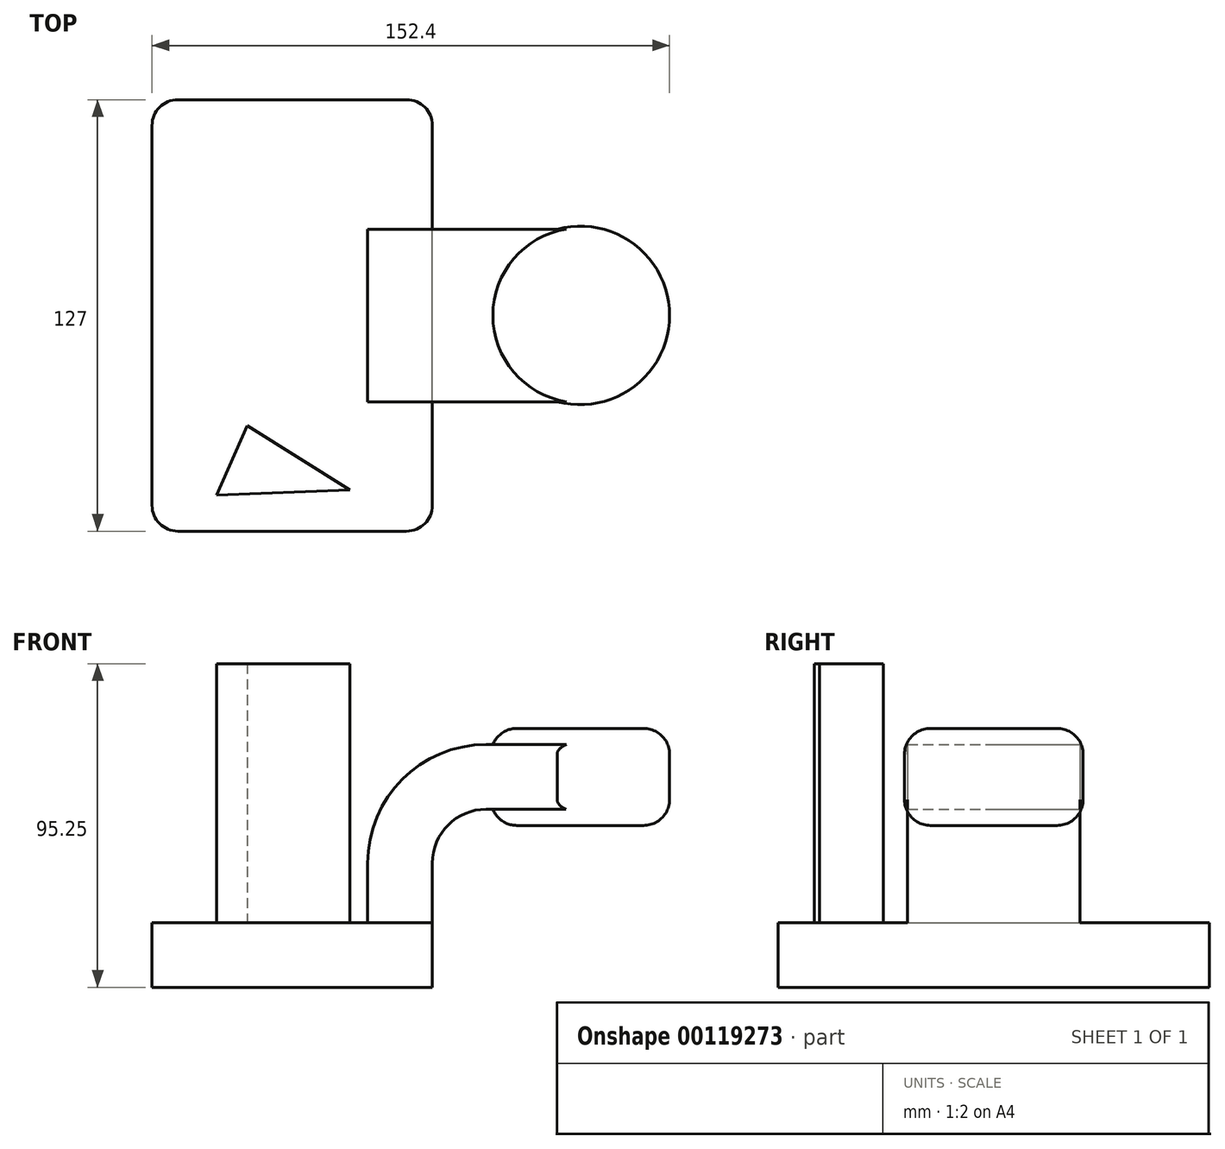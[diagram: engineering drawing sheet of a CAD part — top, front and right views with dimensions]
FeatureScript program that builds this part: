
annotation { "Feature Type Name" : "Feature", "Feature Type Description" : "" }
export const myFeature = defineFeature(function(context is Context, id is Id, definition is map)
    precondition{}
    {
        {
            var Q0;
            Q0=qCreatedBy(makeId("Front.planeOp"),FACE);
            var sketch = newSketch(context, id + "F0", { "sketchPlane" : qUnion([Q0])});
            skLineSegment(sketch, "E0.bottom", {"start": v(-39.2, -9.53) * mm, "end": v(43.35, -9.53) * mm});
            skLineSegment(sketch, "E0.top", {"start": v(-39.2, 9.52) * mm, "end": v(43.35, 9.52) * mm});
            skLineSegment(sketch, "E0.left", {"start": v(-39.2, -9.53) * mm, "end": v(-39.2, 9.52) * mm});
            skLineSegment(sketch, "E0.right", {"start": v(43.35, -9.53) * mm, "end": v(43.35, 9.53) * mm});
            skPoint(sketch, "E0.middle", {"position": v(2.07, 0) * mm});
            skLineSegment(sketch, "E1.bottom", {"start": v(62.4, 38.1) * mm, "end": v(113.2, 38.1) * mm});
            skLineSegment(sketch, "E1.top", {"start": v(62.4, 66.68) * mm, "end": v(113.2, 66.68) * mm});
            skLineSegment(sketch, "E1.left", {"start": v(62.4, 38.1) * mm, "end": v(62.4, 66.68) * mm});
            skLineSegment(sketch, "E1.right", {"start": v(113.2, 38.1) * mm, "end": v(113.2, 66.68) * mm});
            skPoint(sketch, "E1.middle", {"position": v(87.8, 52.39) * mm});
            skLineSegment(sketch, "E2", {"start": v(43.35, 9.53) * mm, "end": v(43.35, 27) * mm});
            skArc(sketch, "E3", {"start": v(43.35, 27) * mm, "mid": v(48, 38.23) * mm, "end": v(59.22, 42.88) * mm});
            skLineSegment(sketch, "E4", {"start": v(59.22, 42.88) * mm, "end": v(86.9, 42.88) * mm});
            skLineSegment(sketch, "E5.0", {"start": v(59.22, 61.93) * mm, "end": v(86.9, 61.93) * mm});
            skArc(sketch, "E5.1", {"start": v(24.3, 27) * mm, "mid": v(34.53, 51.7) * mm, "end": v(59.22, 61.93) * mm});
            skLineSegment(sketch, "E5.2", {"start": v(24.3, 9.53) * mm, "end": v(24.3, 27) * mm});
            skLineSegment(sketch, "E6", {"start": v(86.9, 42.88) * mm, "end": v(86.9, 61.93) * mm});
            skFitSpline(sketch, "E7", {"points": [v(-39.2, 9.53) * mm, v(59.22, 61.93) * mm], "startDerivative": vector(37.18, 98.5) * mm, "endDerivative": vector(113.48, -14.04) * mm});
            skLineSegment(sketch, "E8", {"start": v(86.9, 61.93) * mm, "end": v(86.9, 66.68) * mm});
            skLineSegment(sketch, "E9", {"start": v(86.9, 66.68) * mm, "end": v(86.9, 38.1) * mm});
            skSolve(sketch);
        }
        {
            var Q0;
            Q0=makeQuery(id+"F0.imprint","IMPRINT",FACE,{"disambiguationData":[TD([[makeQuery(id+"F0.imprint","IMPRINT",EDGE,{"derivedFrom":sQuery(id+"F0.wireOp",EDGE,"E0.bottom")}),1.0]])]});
            extrude(context, id + "F1", {"entities" : qUnion([Q0]), "endBound" : BoundingType.SYMMETRIC, "depth" : 127 * mm});
        }
        {
            var Q0;
            {var subQ1=sQuery(id+"F0.wireOp",EDGE,"E2");Q0=makeQuery(id+"F0.imprint","IMPRINT",FACE,{"disambiguationData":[TD([[makeQuery(id+"F0.imprint","IMPRINT",EDGE,{"derivedFrom":subQ1}),1.0]])]});}
            extrude(context, id + "F2", {"entities" : qUnion([Q0]), "operationType" : NewBodyOperationType.ADD, "endBound" : BoundingType.SYMMETRIC, "depth" : 50.8 * mm});
        }
        {
            var Q0;
            Q0=makeQuery(id+"F0.imprint","IMPRINT",FACE,{"disambiguationData":[TD([[makeQuery(id+"F0.imprint","IMPRINT",EDGE,{"derivedFrom":sQuery(id+"F0.wireOp",EDGE,"E5.1")}),1.0]])]});
            extrude(context, id + "F3", {"entities" : qUnion([Q0]), "operationType" : NewBodyOperationType.ADD, "endBound" : BoundingType.SYMMETRIC, "depth" : 15.88 * mm});
        }
        {
            var Q0;
            {var subQ5=sQuery(id+"F0.wireOp",EDGE,"E6");Q0=makeQuery(id+"F0.imprint","IMPRINT",FACE,{"disambiguationData":[TD([[makeQuery(id+"F0.imprint","IMPRINT",EDGE,{"derivedFrom":subQ5}),1.0]])]});}
            extrude(context, id + "F4", {"entities" : qUnion([Q0]), "operationType" : NewBodyOperationType.ADD, "endBound" : BoundingType.SYMMETRIC, "depth" : 50.8 * mm});
        }
        {
            var Q0;
            {var subQ0=sQuery(id+"F0.wireOp",EDGE,"E1.right");Q0=makeQuery(id+"F0.imprint","IMPRINT",FACE,{"disambiguationData":[TD([[makeQuery(id+"F0.imprint","IMPRINT",EDGE,{"derivedFrom":subQ0}),1.0]])]});}
            var Q1;
            Q1=sQuery(id+"F0.wireOp",EDGE,"E6");
            revolve(context, id + "F5", {"operationType" : NewBodyOperationType.ADD, "entities" : qUnion([Q0]), "axis" : qUnion([Q1]), "revolveType" : RevolveType.FULL});
        }
        {
            var Q0;
            Q0=makeQuery(id+"F1.opExtrude","CAP_EDGE",EDGE,{"disambiguationData":[OSD([sQuery(id+"F0.wireOp",EDGE,"E0.right")])],"isStart":true});
            var Q1;
            Q1=makeQuery(id+"F1.opExtrude","CAP_EDGE",EDGE,{"disambiguationData":[OSD([sQuery(id+"F0.wireOp",EDGE,"E0.left")])],"isStart":true});
            var Q2;
            Q2=makeQuery(id+"F1.opExtrude","CAP_EDGE",EDGE,{"disambiguationData":[OSD([sQuery(id+"F0.wireOp",EDGE,"E0.left")])],"isStart":false});
            var Q3;
            Q3=makeQuery(id+"F1.opExtrude","CAP_EDGE",EDGE,{"disambiguationData":[OSD([sQuery(id+"F0.wireOp",EDGE,"E0.right")])],"isStart":false});
            var Q4;
            Q4=makeQuery(id+"F5.opRevolve","SWEPT_EDGE",EDGE,{"disambiguationData":[OSD([sQuery(id+"F0.wireOp",EDGE,"E1.top"),sQuery(id+"F0.wireOp",EDGE,"E1.right")])]});
            var Q5;
            Q5=makeQuery(id+"F2.opExtrude","CAP_EDGE",EDGE,{"disambiguationData":[OSD([sQuery(id+"F0.wireOp",EDGE,"E1.left")])],"isStart":false});
            var Q6;
            Q6=makeQuery(id+"F5.opRevolve","SWEPT_EDGE",EDGE,{"disambiguationData":[OSD([sQuery(id+"F0.wireOp",EDGE,"E1.bottom"),sQuery(id+"F0.wireOp",EDGE,"E1.right")])]});
            var Q7;
            Q7=makeQuery(id+"F2.opExtrude","CAP_EDGE",EDGE,{"disambiguationData":[OSD([sQuery(id+"F0.wireOp",EDGE,"E1.left")])],"isStart":true});
            fillet(context, id + "F6", {"entities" : qUnion([Q0, Q1, Q2, Q3, Q4, Q5, Q6, Q7]), "radius" : 7.62 * mm, "tangentPropagation" : true, "allowEdgeOverflow" : false});
        }
        {
            var Q0;
            {var subQ3=sQuery(id+"F0.wireOp",EDGE,"E0.top");var subQ4=sQuery(id+"F0.wireOp",EDGE,"E0.right");var subQ5=sQuery(id+"F0.wireOp",EDGE,"E0.left");Q0=makeQuery(id+"F3.boolean.opBoolean","SPLIT",FACE,{"disambiguationData":[TD([makeQuery(id+"F1.opExtrude","CAP_FACE",FACE,{"disambiguationData":[OSD([sQuery(id+"F0.wireOp",EDGE,"E0.bottom"),subQ3,subQ5,subQ4])],"isStart":false})])],"derivedFrom":makeQuery(id+"F1.opExtrude","SWEPT_FACE",FACE,{"disambiguationData":[OSD([subQ3])]})});}
            var sketch = newSketch(context, id + "F7", { "sketchPlane" : qUnion([Q0])});
            skLineSegment(sketch, "E10", {"start": v(-11.15, -32.5) * mm, "end": v(19.07, -51.4) * mm});
            skLineSegment(sketch, "E11", {"start": v(-11.15, -32.5) * mm, "end": v(-20.22, -52.91) * mm});
            skLineSegment(sketch, "E12", {"start": v(-20.22, -52.91) * mm, "end": v(19.07, -51.4) * mm});
            skSolve(sketch);
        }
        {
            var Q0;
            Q0 = qSketchRegion(id + "F7", true);
            extrude(context, id + "F8", {"entities" : qUnion([Q0]), "operationType" : NewBodyOperationType.ADD, "depth" : 76.2 * mm});
        }
    });
